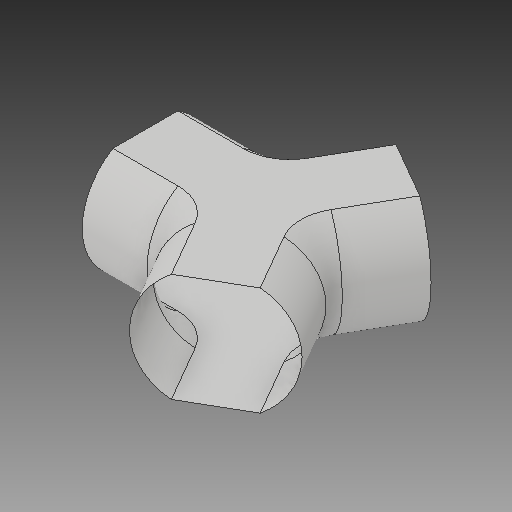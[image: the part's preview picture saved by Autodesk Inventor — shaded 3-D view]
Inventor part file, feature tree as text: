
AUTODESK INVENTOR PART (.ipt)
format: ipt  version: 2017 (Build 210142000, 142)  size: 192,512 bytes
history: native  units: in
note: dims shown in document units (in); Inventor stores cm internally (conversion verified against a paired STEP export)
features: sketch x3, extrude x2, other x2, pattern_circular x2, sweep x1, delete_face x1
ambient origin geometry x8: Origin, YZ Plane, XZ Plane, XY Plane, X Axis, Y Axis, Z Axis, Center Point
bodies: Solid1 (feature_tree)
feature tree (11):
  sketch  "Sketch1"  dims[d10=6.6667in d12=4.0in d13=0.0in d15=2.8217in d16=1.1811in d17=360.0deg]
  extrude  "corridor"  Depth=6.6667in
  other  "found rotaion axis"
  other  "rotaion axis"
  pattern_circular  "other corridors"  Count=3 Angle=360.0deg
  sketch  "Sketch5"  dims[d105=4.0in d107=3.8873in d108=3.8873in d112=1.6458in d118=3.3333in d120=1.0in d121=0.0in]
  sketch  "Sketch4"  dims[d24=0.0in d25=0.0in d26=1.1811in d27=360.0deg]
  sweep  "curve edjes"
  pattern_circular  "repeat curve edjes"  [2 undecoded]
  extrude  "hole fill in"  [1 undecoded]
  delete_face  "Delete Face1"
note: 3 required parameter values undecoded (feature->parameter linkage not recoverable at this tier; creation-order binding heuristic only, values carry confidence <= 0.55)
